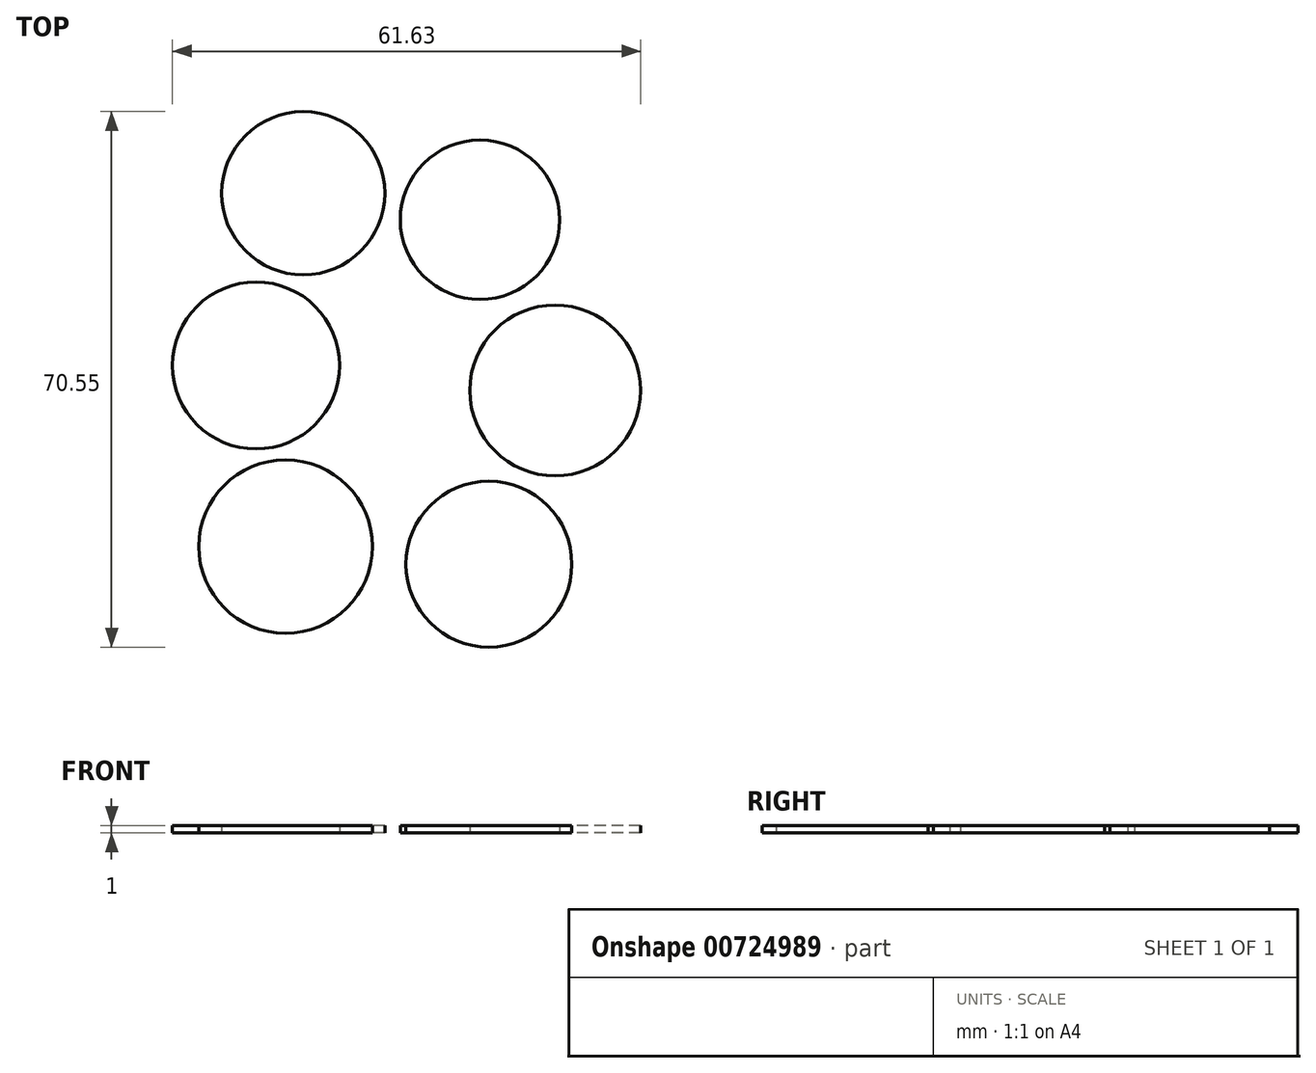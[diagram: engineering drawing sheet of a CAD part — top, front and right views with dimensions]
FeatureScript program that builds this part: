
annotation { "Feature Type Name" : "Feature", "Feature Type Description" : "" }
export const myFeature = defineFeature(function(context is Context, id is Id, definition is map)
    precondition{}
    {
        {
            var Q0;
            Q0=qCreatedBy(makeId("Top.planeOp"),FACE);
            var sketch = newSketch(context, id + "F0", { "sketchPlane" : qUnion([Q0])});
            skCircle(sketch, "E0", {"center": v(-19.3, 5.53) * mm, "radius": 11 * mm});
            skCircle(sketch, "E1", {"center": v(20.08, 2.23) * mm, "radius": 11.25 * mm});
            skCircle(sketch, "E2", {"center": v(-15.42, -18.33) * mm, "radius": 11.43 * mm});
            skCircle(sketch, "E3", {"center": v(10.18, 24.73) * mm, "radius": 10.5 * mm});
            skCircle(sketch, "E4", {"center": v(-13.1, 28.22) * mm, "radius": 10.75 * mm});
            skCircle(sketch, "E5", {"center": v(11.35, -20.66) * mm, "radius": 10.93 * mm});
            skSolve(sketch);
        }
        {
            var Q0;
            Q0=makeQuery(id+"F0.imprint","IMPRINT",FACE,{"disambiguationData":[TD([[makeQuery(id+"F0.imprint","IMPRINT",EDGE,{"derivedFrom":sQuery(id+"F0.wireOp",EDGE,"E5")}),1.0]])]});
            var Q1;
            Q1=makeQuery(id+"F0.imprint","IMPRINT",FACE,{"disambiguationData":[TD([[makeQuery(id+"F0.imprint","IMPRINT",EDGE,{"derivedFrom":sQuery(id+"F0.wireOp",EDGE,"E1")}),1.0]])]});
            var Q2;
            Q2=makeQuery(id+"F0.imprint","IMPRINT",FACE,{"disambiguationData":[TD([[makeQuery(id+"F0.imprint","IMPRINT",EDGE,{"derivedFrom":sQuery(id+"F0.wireOp",EDGE,"E3")}),1.0]])]});
            var Q3;
            Q3=makeQuery(id+"F0.imprint","IMPRINT",FACE,{"disambiguationData":[TD([[makeQuery(id+"F0.imprint","IMPRINT",EDGE,{"derivedFrom":sQuery(id+"F0.wireOp",EDGE,"E4")}),1.0]])]});
            var Q4;
            Q4=makeQuery(id+"F0.imprint","IMPRINT",FACE,{"disambiguationData":[TD([[makeQuery(id+"F0.imprint","IMPRINT",EDGE,{"derivedFrom":sQuery(id+"F0.wireOp",EDGE,"E0")}),1.0]])]});
            var Q5;
            Q5=makeQuery(id+"F0.imprint","IMPRINT",FACE,{"disambiguationData":[TD([[makeQuery(id+"F0.imprint","IMPRINT",EDGE,{"derivedFrom":sQuery(id+"F0.wireOp",EDGE,"E2")}),1.0]])]});
            extrude(context, id + "F1", {"entities" : qUnion([Q0, Q1, Q2, Q3, Q4, Q5]), "depth" : 1 * mm, "offsetDistance" : 25 * mm});
        }
    });
